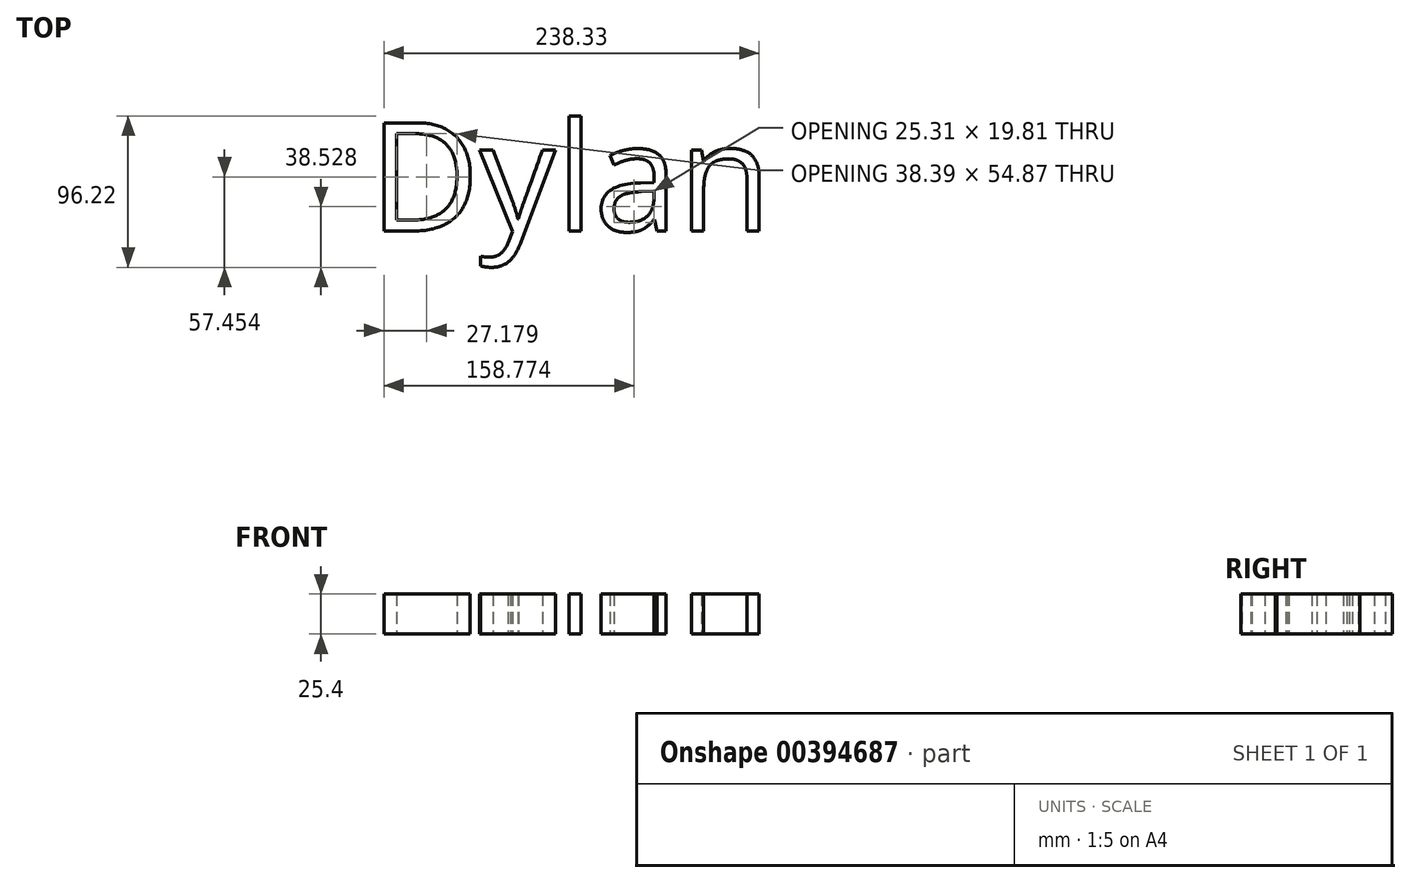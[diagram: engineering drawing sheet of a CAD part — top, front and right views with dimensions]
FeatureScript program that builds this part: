
annotation { "Feature Type Name" : "Feature", "Feature Type Description" : "" }
export const myFeature = defineFeature(function(context is Context, id is Id, definition is map)
    precondition{}
    {
        {
            var Q0;
            Q0=qCreatedBy(makeId("Top.planeOp"),FACE);
            var sketch = newSketch(context, id + "F0", { "sketchPlane" : qUnion([Q0])});
            skText(sketch, "E0", { "text": "Dylan", "fontName": "OpenSans-Regular.ttf"});
            const initialGuessF0  = {"E0": [-0.6657, -0.05652, 1, 0, 0.06927]};
            skSetInitialGuess(sketch, initialGuessF0);
            skSolve(sketch);
        }
        {
            var Q0;
            Q0 = qSketchRegion(id + "F0", true);
            extrude(context, id + "F1", {"entities" : qUnion([Q0]), "depth" : 25.4 * mm});
        }
    });
